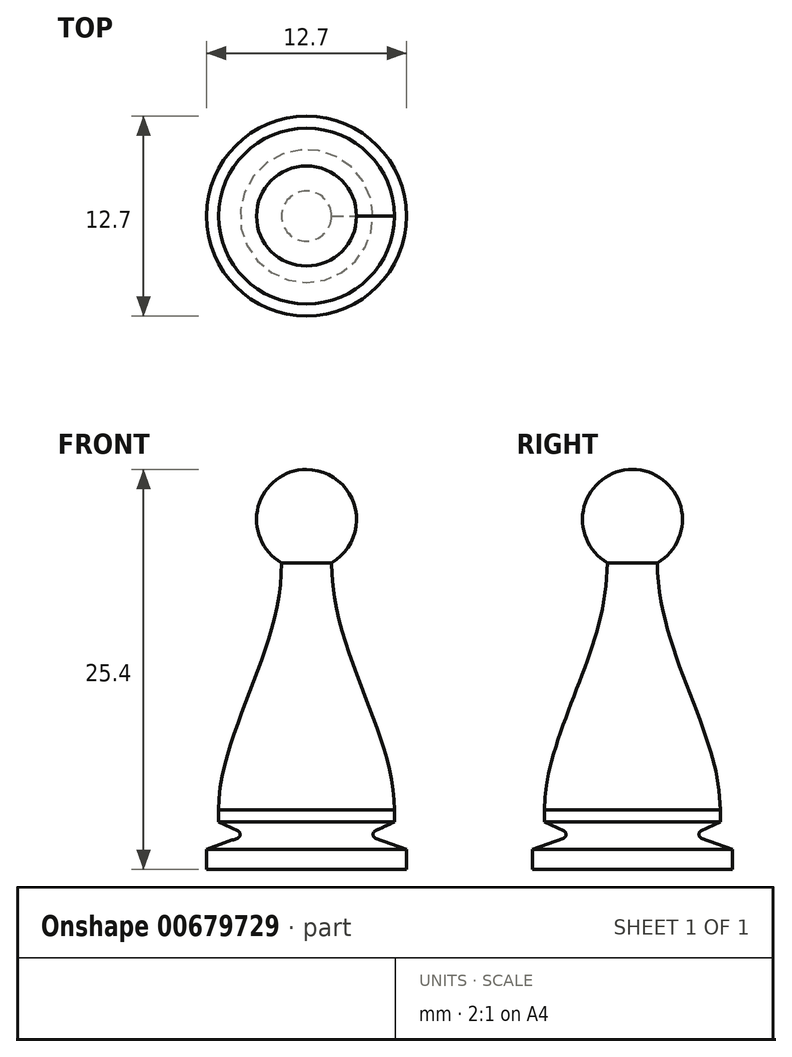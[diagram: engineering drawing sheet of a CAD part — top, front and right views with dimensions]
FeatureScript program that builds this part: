
annotation { "Feature Type Name" : "Feature", "Feature Type Description" : "" }
export const myFeature = defineFeature(function(context is Context, id is Id, definition is map)
    precondition{}
    {
        {
            var Q0;
            Q0=qCreatedBy(makeId("Front.planeOp"),FACE);
            var sketch = newSketch(context, id + "F0", { "sketchPlane" : qUnion([Q0])});
            skLineSegment(sketch, "E0", {"start": v(0, 25.4) * mm, "end": v(0, 0) * mm});
            skLineSegment(sketch, "E1", {"start": v(-6.35, 0) * mm, "end": v(-3.81, 0) * mm});
            skLineSegment(sketch, "E2", {"start": v(-6.35, 0) * mm, "end": v(-6.35, 1.27) * mm});
            skLineSegment(sketch, "E3", {"start": v(6.35, 0) * mm, "end": v(6.35, 1.27) * mm});
            skLineSegment(sketch, "E4", {"start": v(-1.59, 19.48) * mm, "end": v(1.59, 19.48) * mm, "construction": true});
            skArc(sketch, "E5", {"start": v(-1.59, 19.48) * mm, "mid": v(0, 19.05) * mm, "end": v(1.59, 19.48) * mm, "construction": true});
            skArc(sketch, "E6", {"start": v(1.59, 19.48) * mm, "mid": v(0, 25.4) * mm, "end": v(-1.59, 19.48) * mm});
            skLineSegment(sketch, "E7", {"start": v(-1.59, 19.48) * mm, "end": v(-6.35, 0) * mm, "construction": true});
            skLineSegment(sketch, "E8", {"start": v(1.59, 19.48) * mm, "end": v(6.35, 0) * mm, "construction": true});
            skLineSegment(sketch, "E9", {"start": v(-6.35, 1.27) * mm, "end": v(-3.81, 2.2) * mm});
            skLineSegment(sketch, "E10", {"start": v(6.35, 1.27) * mm, "end": v(3.8, 2.2) * mm});
            skLineSegment(sketch, "E11", {"start": v(3.8, 2.2) * mm, "end": v(5.59, 3.02) * mm});
            skLineSegment(sketch, "E12", {"start": v(-3.81, 2.2) * mm, "end": v(-3.81, 0) * mm, "construction": true});
            skLineSegment(sketch, "E13", {"start": v(3.81, 2.2) * mm, "end": v(3.81, 0) * mm, "construction": true});
            skLineSegment(sketch, "E14", {"start": v(5.59, 3.02) * mm, "end": v(5.59, 3.79) * mm});
            skLineSegment(sketch, "E15", {"start": v(-3.81, 2.2) * mm, "end": v(-5.59, 3.02) * mm});
            skLineSegment(sketch, "E16", {"start": v(-5.59, 3.02) * mm, "end": v(-5.59, 3.79) * mm});
            skFitSpline(sketch, "E17", {"points": [v(-1.59, 19.48) * mm, v(-5.59, 3.79) * mm], "startDerivative": vector(0, -16.95) * mm, "endDerivative": vector(0, -14.6) * mm});
            skFitSpline(sketch, "E18", {"points": [v(1.59, 19.48) * mm, v(5.59, 3.79) * mm], "startDerivative": vector(0, -16.95) * mm, "endDerivative": vector(0, -14.6) * mm});
            skLineSegment(sketch, "E19", {"start": v(-1.59, 19.48) * mm, "end": v(-1.59, 20.7) * mm, "construction": true});
            skLineSegment(sketch, "E20", {"start": v(1.59, 19.48) * mm, "end": v(1.59, 20.67) * mm, "construction": true});
            skLineSegment(sketch, "E21", {"start": v(-1.59, 13.83) * mm, "end": v(1.59, 13.83) * mm, "construction": true});
            skLineSegment(sketch, "E22", {"start": v(-5.59, 8.65) * mm, "end": v(5.59, 8.65) * mm, "construction": true});
            skPoint(sketch, "E23", {"position": v(0, 8.65) * mm});
            skLineSegment(sketch, "E24", {"start": v(-3.81, 0) * mm, "end": v(3.81, 0) * mm});
            skLineSegment(sketch, "E25", {"start": v(3.81, 0) * mm, "end": v(6.35, 0) * mm});
            skFitSpline(sketch, "E26", {"points": [v(5.59, 3.02) * mm, v(3.81, 2.2) * mm, v(6.35, 1.27) * mm], "startDerivative": vector(0, -4.81) * mm, "endDerivative": vector(0, -5.64) * mm, "construction": true});
            skFitSpline(sketch, "E27", {"points": [v(-5.59, 3.02) * mm, v(-3.81, 2.2) * mm, v(-6.35, 1.27) * mm], "startDerivative": vector(0, -4.81) * mm, "endDerivative": vector(0, -5.64) * mm, "construction": true});
            skLineSegment(sketch, "E28", {"start": v(-5.59, 2.29) * mm, "end": v(5.59, 2.29) * mm, "construction": true});
            skLineSegment(sketch, "E29", {"start": v(-6.35, 2.29) * mm, "end": v(6.35, 2.29) * mm, "construction": true});
            skSolve(sketch);
        }
        {
            var Q0;
            {var subQ1=sQuery(id+"F0.wireOp",EDGE,"E0");Q0=makeQuery(id+"F0.imprint","IMPRINT",FACE,{"disambiguationData":[TD([[makeQuery(id+"F0.imprint","IMPRINT",EDGE,{"derivedFrom":subQ1}),1.0]])]});}
            var Q1;
            Q1=sQuery(id+"F0.wireOp",EDGE,"E0");
            revolve(context, id + "F1", {"entities" : qUnion([Q0]), "axis" : qUnion([Q1]), "revolveType" : RevolveType.FULL});
        }
        {
            var Q0;
            Q0=makeQuery(id+"F1.opRevolve","SWEPT_EDGE",EDGE,{"disambiguationData":[OSD([sQuery(id+"F0.wireOp",EDGE,"E10"),sQuery(id+"F0.wireOp",EDGE,"E11")])]});
            fillet(context, id + "F2", {"entities" : qUnion([Q0]), "radius" : 0.25 * mm, "allowEdgeOverflow" : false});
        }
    });
